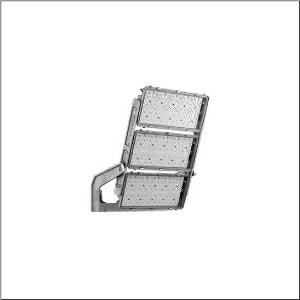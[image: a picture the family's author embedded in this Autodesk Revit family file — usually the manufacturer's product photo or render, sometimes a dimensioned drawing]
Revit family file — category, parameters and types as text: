
# Revit family: floodlight_fl_11_maxi_pro_remote___pl64blc_5xa779425w01aa_643d
name_source: partatom
category: Lighting Fixtures
units: mm (PartAtom-declared; Revit-internal decimal feet)

## family parameters
Cut with Voids When Loaded = No
Host = Face
Light Source = No
Part Type = Normal
Room Calculation Point = No
Round Connector Dimension = Use Diameter
Shared = No

## types (1)
- --- (1 x LED, 135060 lm, 1516.7 W, 3000K)
    Apparent Load = 1517 VA
    CIE Flux Codes = 28 83 99 100 100
    Color Rendering = 70
    Color Temperature = 3000K
    Default Elevation = 1800 mm
    Description = Floodlight FL 11  maxi  pro Remote floodlight; light control with lens of PMMA; cover panel of toughened safety glass, transparent; light distribution: PL64BLC, asymmetric direct distribution, LEDcolour temperature: 3000K, rated luminous flux: 135.060lm, colour rendering: CRI > 70, light colour: 730; luminous efficacy: 89lm/W; brightness control: DALI 2 (1 DALI address); with terminal, 8-pole, max. 2.5mm², mains connection: 220..240V/380..400V AC, 50/60Hz, surge voltage resistance: line to ground: 10kV, ECG replaceable separately, no afterglow with DALI off / DMX off command, LED unit replaceable without ESD environment, dustproof LED module, dimming range 10..100%; 1517W floodlight with 2x LED unit of diecast aluminium, coated grey; length: 713mm / width: 651mm / height: 338mm; mounting bracket, of diecast aluminium, uncoated, natural, equipment: Power, protection rating (complete): IP66; insulation class (complete): insulation class I (protective earthing); certification: CE, ENEC, VDE; ball protection: ball impact resistance with accessories, impact resistance: IK07; only for outdoor installations, rated ambient temperature 10°C, permissible operating ambient temperature: -40..+30°C, permissible storage temperature: -40..+85°Cpackaging unit: 1 piece

Light Distribution: PL64BLC
    Height = 320 mm
    Lamp = 1 x LED
    Lamp Light Flux = 135060 lm
    Lamp Power = 1516.7 W
    Lamp count = 1
    Length = 1002 mm
    Luminous efficacy = 89 lm/W
    Manufacturer = Siteco
    ModVariant = No
    Model = 5XA779425W01AA
    Mounting Place = Ceiling
    Mounting Type = Surface mounted
    Number of Poles = 1
    OnlyDefault = Yes
    Power Factor = 1
    Product Name = Floodlight FL 11 maxi pro Remote | PL64BLC
    Product group = floodlight | ceiling mounted
    ProductGroupID = 301
    Protection Class = Protection class I
    Protection Degree = IP 66
    RLX_Detail_Level = 1
    RLX_Emergency_Light_Flux = 0 lm
    RLX_Emergency_Type = 0
    RLX_Emergency_Type_DB = No
    RlxData = <blob elided: 52081 chars, md5=8b8f1a2f>
    Socket = socket
    Standby Power = 0 W
    System Light Flux = 135060 lm
    System Power = 1517 W
    Type Comments = factory setting: luminous flux: 100 % | dim-lin: 254 | 1070 mA
    Type Image = l_1349141.jpg
    URL = http://relux.com
    VarID = @adj_080820
    Voltage = 0 V
    Weight = 0.00 kg
    Width = 655 mm

## geometry (parser evidence)
native form markers: Blend x4, Sweep x12
no freeform markers — native parametric forms only
